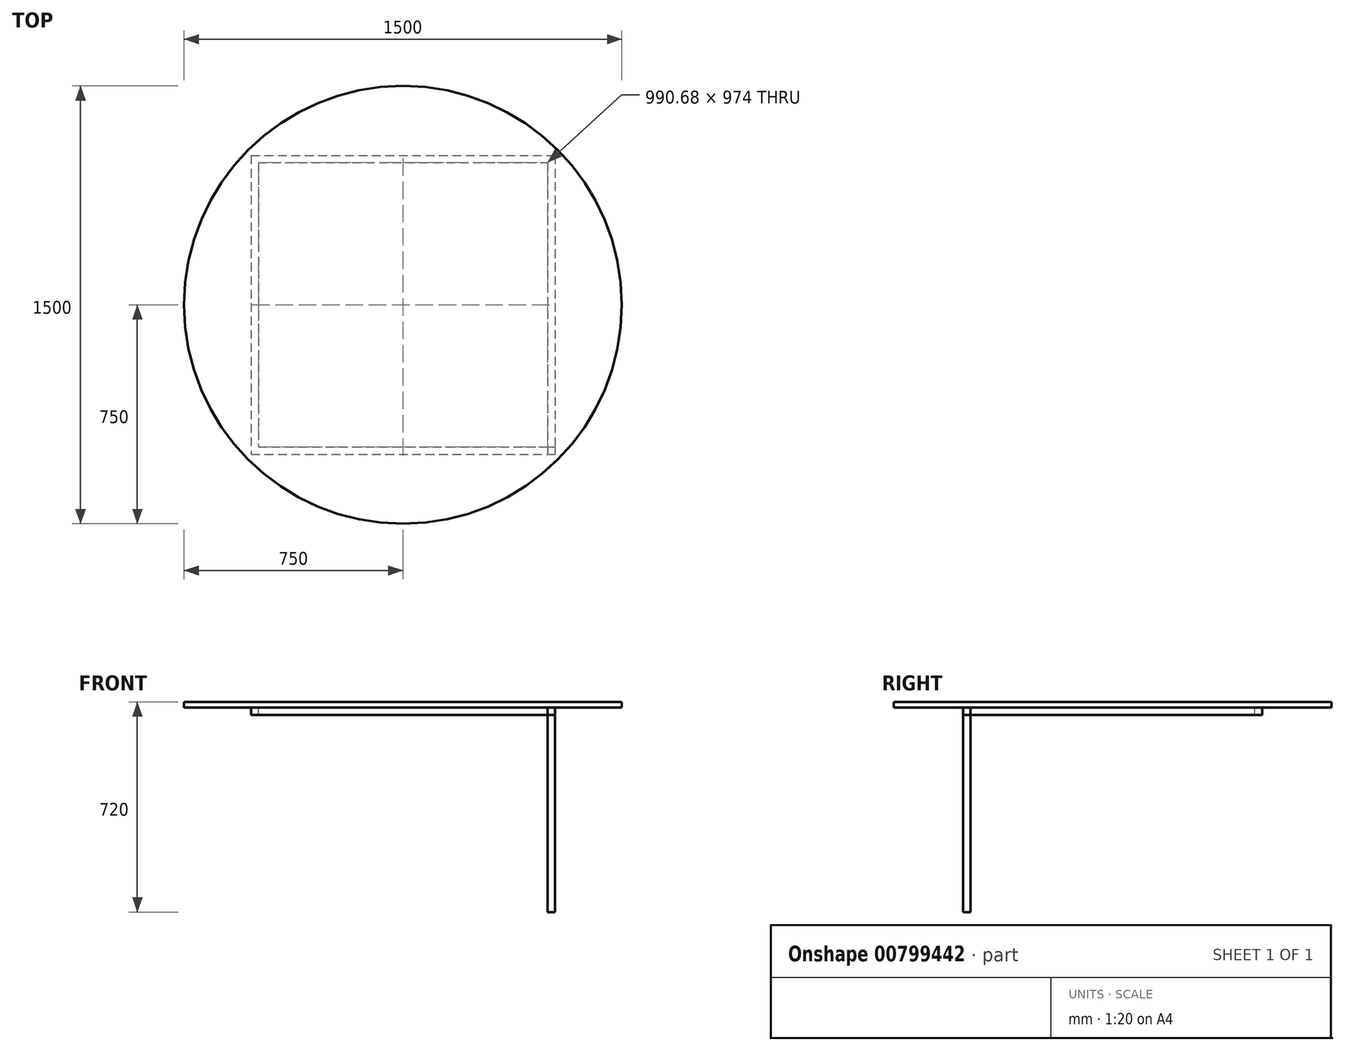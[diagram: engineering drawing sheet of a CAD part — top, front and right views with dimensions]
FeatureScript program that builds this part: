
annotation { "Feature Type Name" : "Feature", "Feature Type Description" : "" }
export const myFeature = defineFeature(function(context is Context, id is Id, definition is map)
    precondition{}
    {
        {
            var Q0;
            Q0=qCreatedBy(makeId("Top.planeOp"),FACE);
            var sketch = newSketch(context, id + "F0", { "sketchPlane" : qUnion([Q0])});
            skCircle(sketch, "E0", {"center": v(0, 0) * mm, "radius": 750 * mm});
            skCircle(sketch, "E1", {"center": v(0, 0) * mm, "radius": 730 * mm});
            skLineSegment(sketch, "E2.rect.bottom", {"start": v(-520.34, 512) * mm, "end": v(520.34, 512) * mm});
            skLineSegment(sketch, "E2.rect.top", {"start": v(-520.34, -512) * mm, "end": v(520.34, -512) * mm});
            skLineSegment(sketch, "E2.rect.left", {"start": v(-520.34, 512) * mm, "end": v(-520.34, -512) * mm});
            skLineSegment(sketch, "E2.rect.right", {"start": v(520.34, 512) * mm, "end": v(520.34, -512) * mm});
            skLineSegment(sketch, "E3.rect.bottom", {"start": v(-495.34, 487) * mm, "end": v(495.34, 487) * mm});
            skLineSegment(sketch, "E3.rect.top", {"start": v(-495.34, -487) * mm, "end": v(495.34, -487) * mm});
            skLineSegment(sketch, "E3.rect.left", {"start": v(-495.34, 487) * mm, "end": v(-495.34, -487) * mm});
            skLineSegment(sketch, "E3.rect.right", {"start": v(495.34, 487) * mm, "end": v(495.34, -487) * mm});
            skLineSegment(sketch, "E4.bottom", {"start": v(-520.34, 512) * mm, "end": v(-495.34, 512) * mm});
            skLineSegment(sketch, "E4.top", {"start": v(-520.34, 487) * mm, "end": v(-495.34, 487) * mm});
            skLineSegment(sketch, "E4.left", {"start": v(-520.34, 512) * mm, "end": v(-520.34, 487) * mm});
            skLineSegment(sketch, "E4.right", {"start": v(-495.34, 512) * mm, "end": v(-495.34, 487) * mm});
            skLineSegment(sketch, "E5.bottom", {"start": v(520.34, 512) * mm, "end": v(495.34, 512) * mm});
            skLineSegment(sketch, "E5.top", {"start": v(520.34, 487) * mm, "end": v(495.34, 487) * mm});
            skLineSegment(sketch, "E5.left", {"start": v(520.34, 512) * mm, "end": v(520.34, 487) * mm});
            skLineSegment(sketch, "E5.right", {"start": v(495.34, 512) * mm, "end": v(495.34, 487) * mm});
            skLineSegment(sketch, "E6.bottom", {"start": v(495.34, -487) * mm, "end": v(520.34, -487) * mm});
            skLineSegment(sketch, "E6.top", {"start": v(495.34, -512) * mm, "end": v(520.34, -512) * mm});
            skLineSegment(sketch, "E6.left", {"start": v(495.34, -487) * mm, "end": v(495.34, -512) * mm});
            skLineSegment(sketch, "E6.right", {"start": v(520.34, -487) * mm, "end": v(520.34, -512) * mm});
            skLineSegment(sketch, "E7.bottom", {"start": v(-520.34, -512) * mm, "end": v(-495.34, -512) * mm});
            skLineSegment(sketch, "E7.top", {"start": v(-520.34, -487) * mm, "end": v(-495.34, -487) * mm});
            skLineSegment(sketch, "E7.left", {"start": v(-520.34, -512) * mm, "end": v(-520.34, -487) * mm});
            skLineSegment(sketch, "E7.right", {"start": v(-495.34, -512) * mm, "end": v(-495.34, -487) * mm});
            skSolve(sketch);
        }
        {
            var Q0;
            Q0=makeQuery(id+"F0.imprint","IMPRINT",FACE,{"disambiguationData":[TD([[makeQuery(id+"F0.imprint","IMPRINT",EDGE,{"derivedFrom":sQuery(id+"F0.wireOp",EDGE,"E7.bottom")}),1.0]])]});
            var Q1;
            Q1=makeQuery(id+"F0.imprint","IMPRINT",FACE,{"disambiguationData":[TD([[makeQuery(id+"F0.imprint","IMPRINT",EDGE,{"derivedFrom":sQuery(id+"F0.wireOp",EDGE,"E6.bottom")}),-1.0]])]});
            var Q2;
            Q2=makeQuery(id+"F0.imprint","IMPRINT",FACE,{"disambiguationData":[TD([[makeQuery(id+"F0.imprint","IMPRINT",EDGE,{"derivedFrom":sQuery(id+"F0.wireOp",EDGE,"E5.bottom")}),1.0]])]});
            var Q3;
            Q3=makeQuery(id+"F0.imprint","IMPRINT",FACE,{"disambiguationData":[TD([[makeQuery(id+"F0.imprint","IMPRINT",EDGE,{"derivedFrom":sQuery(id+"F0.wireOp",EDGE,"E4.bottom")}),-1.0]])]});
            extrude(context, id + "F1", {"entities" : qUnion([Q0, Q1, Q2, Q3]), "oppositeDirection" : true, "depth" : 700 * mm});
        }
        {
            var Q0;
            Q0=makeQuery(id+"F0.imprint","IMPRINT",FACE,{"disambiguationData":[TD([[makeQuery(id+"F0.imprint","IMPRINT",EDGE,{"derivedFrom":sQuery(id+"F0.wireOp",EDGE,"E2.rect.top")}),1.0]])]});
            var Q1;
            Q1=makeQuery(id+"F0.imprint","IMPRINT",FACE,{"disambiguationData":[TD([[makeQuery(id+"F0.imprint","IMPRINT",EDGE,{"derivedFrom":sQuery(id+"F0.wireOp",EDGE,"E2.rect.right")}),-1.0]])]});
            var Q2;
            Q2=makeQuery(id+"F0.imprint","IMPRINT",FACE,{"disambiguationData":[TD([[makeQuery(id+"F0.imprint","IMPRINT",EDGE,{"derivedFrom":sQuery(id+"F0.wireOp",EDGE,"E2.rect.bottom")}),-1.0]])]});
            var Q3;
            Q3=makeQuery(id+"F0.imprint","IMPRINT",FACE,{"disambiguationData":[TD([[makeQuery(id+"F0.imprint","IMPRINT",EDGE,{"derivedFrom":sQuery(id+"F0.wireOp",EDGE,"E2.rect.left")}),1.0]])]});
            extrude(context, id + "F2", {"entities" : qUnion([Q0, Q1, Q2, Q3]), "oppositeDirection" : true, "depth" : 25 * mm});
        }
        {
            var Q0;
            Q0=qCreatedBy(makeId("Top.planeOp"),FACE);
            var sketch = newSketch(context, id + "F3", { "sketchPlane" : qUnion([Q0])});
            skCircle(sketch, "E8", {"center": v(0, 0) * mm, "radius": 750 * mm});
            skSolve(sketch);
        }
        {
            var Q0;
            Q0=makeQuery(id+"F3.imprint","IMPRINT",FACE,{"disambiguationData":[TD([[makeQuery(id+"F3.imprint","IMPRINT",EDGE,{"derivedFrom":sQuery(id+"F3.wireOp",EDGE,"E8")}),1.0]])]});
            extrude(context, id + "F4", {"entities" : qUnion([Q0]), "depth" : 20 * mm});
        }
        {
            var Q0;
            Q0=qCreatedBy(makeId("Top.planeOp"),FACE);
            var sketch = newSketch(context, id + "F5", { "sketchPlane" : qUnion([Q0])});
            skCircle(sketch, "E9", {"center": v(0, 0) * mm, "radius": 750 * mm});
            skSolve(sketch);
        }
        {
            var Q0;
            Q0=makeQuery(id+"F5.imprint","IMPRINT",FACE,{"disambiguationData":[TD([[makeQuery(id+"F5.imprint","IMPRINT",EDGE,{"derivedFrom":sQuery(id+"F5.wireOp",EDGE,"E9")}),1.0]])]});
            extrude(context, id + "F6", {"entities" : qUnion([Q0]), "depth" : 20 * mm});
        }
        {
            var Q0;
            Q0=makeQuery(id+"F6.opExtrude","SWEPT_FACE",FACE,{"disambiguationData":[OSD([sQuery(id+"F5.wireOp",EDGE,"E9")])]});
            fillet(context, id + "F7", {"entities" : qUnion([Q0]), "radius" : 9 * mm, "tangentPropagation" : true, "allowEdgeOverflow" : false});
        }
    });
